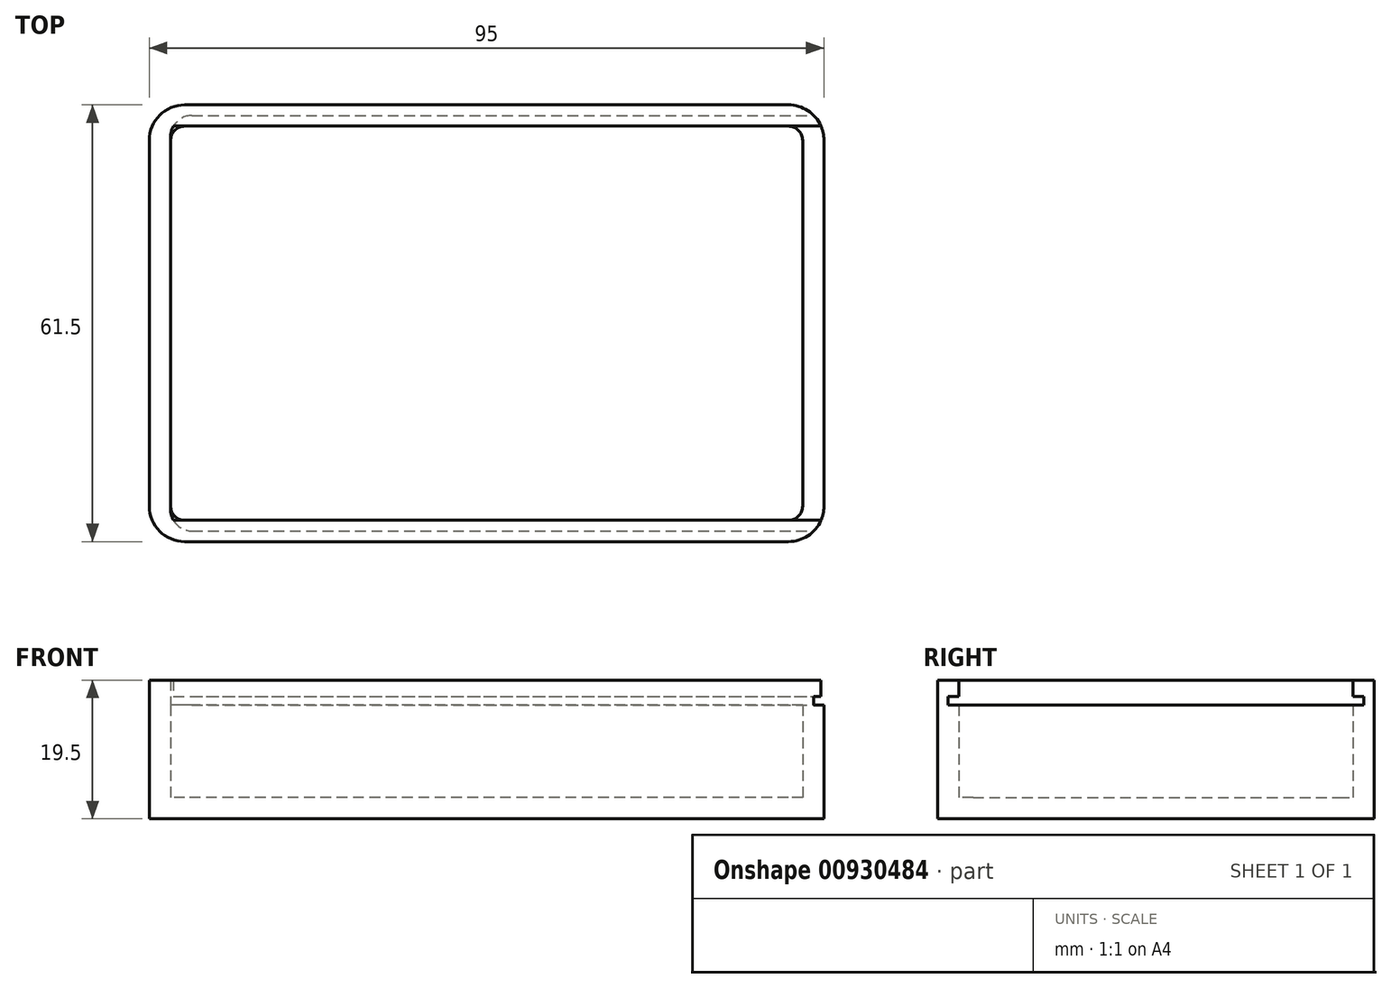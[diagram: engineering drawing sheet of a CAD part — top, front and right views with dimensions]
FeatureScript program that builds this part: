
annotation { "Feature Type Name" : "Feature", "Feature Type Description" : "" }
export const myFeature = defineFeature(function(context is Context, id is Id, definition is map)
    precondition{}
    {
        {
            var Q0;
            Q0=qCreatedBy(makeId("Top.planeOp"),FACE);
            var sketch = newSketch(context, id + "F0", { "sketchPlane" : qUnion([Q0])});
            skLineSegment(sketch, "E0.bottom", {"start": v(44.5, -27.75) * mm, "end": v(-44.5, -27.75) * mm});
            skLineSegment(sketch, "E0.top", {"start": v(44.5, 27.75) * mm, "end": v(-44.5, 27.75) * mm});
            skLineSegment(sketch, "E0.left", {"start": v(44.5, -27.75) * mm, "end": v(44.5, 27.75) * mm});
            skLineSegment(sketch, "E0.right", {"start": v(-44.5, -27.75) * mm, "end": v(-44.5, 27.75) * mm});
            skPoint(sketch, "E0.middle", {"position": v(0, 0) * mm});
            skLineSegment(sketch, "E1.0", {"start": v(47.5, -30.75) * mm, "end": v(47.5, 30.75) * mm});
            skLineSegment(sketch, "E1.1", {"start": v(47.5, -30.75) * mm, "end": v(-47.5, -30.75) * mm});
            skLineSegment(sketch, "E1.2", {"start": v(-47.5, -30.75) * mm, "end": v(-47.5, 30.75) * mm});
            skLineSegment(sketch, "E1.3", {"start": v(47.5, 30.75) * mm, "end": v(-47.5, 30.75) * mm});
            skSolve(sketch);
        }
        {
            var Q0;
            Q0=makeQuery(id+"F0.imprint","IMPRINT",FACE,{"disambiguationData":[TD([[makeQuery(id+"F0.imprint","IMPRINT",EDGE,{"derivedFrom":sQuery(id+"F0.wireOp",EDGE,"E0.bottom")}),-1.0]])]});
            extrude(context, id + "F1", {"entities" : qUnion([Q0]), "depth" : 3 * mm, "offsetDistance" : 25 * mm});
        }
        {
            var Q0;
            Q0=makeQuery(id+"F0.imprint","IMPRINT",FACE,{"disambiguationData":[TD([[makeQuery(id+"F0.imprint","IMPRINT",EDGE,{"derivedFrom":sQuery(id+"F0.wireOp",EDGE,"E0.bottom")}),1.0]])]});
            extrude(context, id + "F2", {"entities" : qUnion([Q0]), "operationType" : NewBodyOperationType.ADD, "depth" : 16 * mm, "offsetDistance" : 25 * mm});
        }
        {
            var Q0;
            Q0=makeQuery(id+"F2.opExtrude","SWEPT_FACE",FACE,{"disambiguationData":[OSD([sQuery(id+"F0.wireOp",EDGE,"E1.0")])]});
            var sketch = newSketch(context, id + "F3", { "sketchPlane" : qUnion([Q0])});
            skLineSegment(sketch, "E2.top", {"start": v(30.75, 16) * mm, "end": v(27.75, 16) * mm});
            skLineSegment(sketch, "E3.top", {"start": v(30.75, 19.5) * mm, "end": v(27.75, 19.5) * mm});
            skLineSegment(sketch, "E3.left", {"start": v(30.75, 16) * mm, "end": v(30.75, 19.5) * mm});
            skLineSegment(sketch, "E3.right", {"start": v(27.75, 17.2) * mm, "end": v(27.75, 19.5) * mm});
            skLineSegment(sketch, "E4", {"start": v(29.6, 17.2) * mm, "end": v(24.82, 17.2) * mm, "construction": true});
            skLineSegment(sketch, "E5", {"start": v(27.75, 17.2) * mm, "end": v(29.25, 17.2) * mm});
            skPoint(sketch, "E5.startSnap0", {"position": v(27.75, 17.75) * mm});
            skLineSegment(sketch, "E6", {"start": v(29.25, 17.2) * mm, "end": v(29.25, 16) * mm});
            skLineSegment(sketch, "E7", {"start": v(0, 27.37) * mm, "end": v(0, -23.35) * mm, "construction": true});
            skLineSegment(sketch, "E8.MirrorCS", {"start": v(-27.75, 17.2) * mm, "end": v(-29.25, 17.2) * mm});
            skLineSegment(sketch, "E9.MirrorCS", {"start": v(-29.25, 17.2) * mm, "end": v(-29.25, 16) * mm});
            skLineSegment(sketch, "E10.MirrorCS", {"start": v(-30.75, 16) * mm, "end": v(-30.75, 19.5) * mm});
            skLineSegment(sketch, "E11.MirrorCS", {"start": v(-30.75, 16) * mm, "end": v(-27.75, 16) * mm});
            skLineSegment(sketch, "E12.MirrorCS", {"start": v(-27.75, 17.2) * mm, "end": v(-27.75, 19.5) * mm});
            skLineSegment(sketch, "E13.MirrorCS", {"start": v(-29.6, 17.2) * mm, "end": v(-24.82, 17.2) * mm, "construction": true});
            skPoint(sketch, "E14.MirrorP", {"position": v(-27.75, 17.75) * mm});
            skLineSegment(sketch, "E15.MirrorCS", {"start": v(-30.75, 19.5) * mm, "end": v(-27.75, 19.5) * mm});
            skLineSegment(sketch, "E16.trimOffspring", {"start": v(-27.75, 16) * mm, "end": v(-30.75, 16) * mm});
            skSolve(sketch);
        }
        {
            var Q0;
            Q0 = qSketchRegion(id + "F3", true);
            var Q1;
            Q1=makeQuery(id+"F2.opExtrude","SWEPT_FACE",FACE,{"disambiguationData":[OSD([sQuery(id+"F0.wireOp",EDGE,"E1.2")])]});
            extrude(context, id + "F4", {"entities" : qUnion([Q0]), "operationType" : NewBodyOperationType.ADD, "endBound" : BoundingType.UP_TO_SURFACE, "oppositeDirection" : true, "depth" : 25 * mm, "endBoundEntityFace" : qUnion([Q1]), "offsetDistance" : 25 * mm});
        }
        {
            var Q0;
            Q0=makeQuery(id+"F4.boolean.opBoolean","MERGE",FACE,{"derivedFrom":[makeQuery(id+"F2.opExtrude","SWEPT_FACE",FACE,{"disambiguationData":[OSD([sQuery(id+"F0.wireOp",EDGE,"E1.2")])]}),makeQuery(id+"F4.opExtrude","CAP_FACE",FACE,{"disambiguationData":[OSD([sQuery(id+"F3.wireOp",EDGE,"E2.top"),sQuery(id+"F3.wireOp",EDGE,"E3.top"),sQuery(id+"F3.wireOp",EDGE,"E3.left"),sQuery(id+"F3.wireOp",EDGE,"E3.right"),sQuery(id+"F3.wireOp",EDGE,"E5"),sQuery(id+"F3.wireOp",EDGE,"E6")])],"isStart":false}),makeQuery(id+"F4.opExtrude","CAP_FACE",FACE,{"disambiguationData":[OSD([sQuery(id+"F3.wireOp",EDGE,"E8.MirrorCS"),sQuery(id+"F3.wireOp",EDGE,"E9.MirrorCS"),sQuery(id+"F3.wireOp",EDGE,"E10.MirrorCS"),sQuery(id+"F3.wireOp",EDGE,"E12.MirrorCS"),sQuery(id+"F3.wireOp",EDGE,"E15.MirrorCS"),sQuery(id+"F3.wireOp",EDGE,"E16.trimOffspring")])],"isStart":false})]});
            var sketch = newSketch(context, id + "F5", { "sketchPlane" : qUnion([Q0])});
            skLineSegment(sketch, "E17.bottom", {"start": v(-30.75, 19.5) * mm, "end": v(30.75, 19.5) * mm});
            skLineSegment(sketch, "E17.top", {"start": v(-30.75, 16) * mm, "end": v(30.75, 16) * mm});
            skLineSegment(sketch, "E17.left", {"start": v(-30.75, 19.5) * mm, "end": v(-30.75, 16) * mm});
            skLineSegment(sketch, "E17.right", {"start": v(30.75, 19.5) * mm, "end": v(30.75, 16) * mm});
            skSolve(sketch);
        }
        {
            var Q0;
            Q0 = qSketchRegion(id + "F5", true);
            var Q1;
            Q1=makeQuery(id+"F2.opExtrude","SWEPT_FACE",FACE,{"disambiguationData":[OSD([sQuery(id+"F0.wireOp",EDGE,"E0.right")])]});
            extrude(context, id + "F6", {"entities" : qUnion([Q0]), "operationType" : NewBodyOperationType.ADD, "oppositeDirection" : true, "depth" : 3 * mm, "endBoundEntityFace" : qUnion([Q1]), "offsetDistance" : 25 * mm});
        }
        {
            var Q0;
            Q0=makeQuery(id+"F4.boolean.opBoolean","MERGE",EDGE,{"derivedFrom":[makeQuery(id+"F2.opExtrude","SWEPT_EDGE",EDGE,{"disambiguationData":[OSD([sQuery(id+"F0.wireOp",EDGE,"E1.0"),sQuery(id+"F0.wireOp",EDGE,"E1.1")])]}),makeQuery(id+"F4.opExtrude","CAP_EDGE",EDGE,{"disambiguationData":[OSD([sQuery(id+"F3.wireOp",EDGE,"E10.MirrorCS")])],"isStart":true})]});
            var Q1;
            Q1=makeQuery(id+"F4.boolean.opBoolean","MERGE",EDGE,{"derivedFrom":[makeQuery(id+"F2.opExtrude","SWEPT_EDGE",EDGE,{"disambiguationData":[OSD([sQuery(id+"F0.wireOp",EDGE,"E1.1"),sQuery(id+"F0.wireOp",EDGE,"E1.2")])]}),makeQuery(id+"F4.opExtrude","CAP_EDGE",EDGE,{"disambiguationData":[OSD([sQuery(id+"F3.wireOp",EDGE,"E10.MirrorCS")])],"isStart":false})]});
            var Q2;
            Q2=makeQuery(id+"F4.boolean.opBoolean","MERGE",EDGE,{"derivedFrom":[makeQuery(id+"F2.opExtrude","SWEPT_EDGE",EDGE,{"disambiguationData":[OSD([sQuery(id+"F0.wireOp",EDGE,"E1.0"),sQuery(id+"F0.wireOp",EDGE,"E1.3")])]}),makeQuery(id+"F4.opExtrude","CAP_EDGE",EDGE,{"disambiguationData":[OSD([sQuery(id+"F3.wireOp",EDGE,"E3.left")])],"isStart":true})]});
            var Q3;
            Q3=makeQuery(id+"F4.boolean.opBoolean","MERGE",EDGE,{"derivedFrom":[makeQuery(id+"F2.opExtrude","SWEPT_EDGE",EDGE,{"disambiguationData":[OSD([sQuery(id+"F0.wireOp",EDGE,"E1.2"),sQuery(id+"F0.wireOp",EDGE,"E1.3")])]}),makeQuery(id+"F4.opExtrude","CAP_EDGE",EDGE,{"disambiguationData":[OSD([sQuery(id+"F3.wireOp",EDGE,"E3.left")])],"isStart":false})]});
            fillet(context, id + "F7", {"entities" : qUnion([Q0, Q1, Q2, Q3]), "radius" : 5 * mm, "tangentPropagation" : true, "allowEdgeOverflow" : false});
        }
        {
            var Q0;
            Q0=makeQuery(id+"F2.opExtrude","SWEPT_EDGE",EDGE,{"disambiguationData":[OSD([sQuery(id+"F0.wireOp",EDGE,"E0.top"),sQuery(id+"F0.wireOp",EDGE,"E0.right")])]});
            var Q1;
            Q1=makeQuery(id+"F2.opExtrude","SWEPT_EDGE",EDGE,{"disambiguationData":[OSD([sQuery(id+"F0.wireOp",EDGE,"E0.bottom"),sQuery(id+"F0.wireOp",EDGE,"E0.right")])]});
            var Q2;
            Q2=makeQuery(id+"F2.opExtrude","SWEPT_EDGE",EDGE,{"disambiguationData":[OSD([sQuery(id+"F0.wireOp",EDGE,"E0.bottom"),sQuery(id+"F0.wireOp",EDGE,"E0.left")])]});
            var Q3;
            Q3=makeQuery(id+"F2.opExtrude","SWEPT_EDGE",EDGE,{"disambiguationData":[OSD([sQuery(id+"F0.wireOp",EDGE,"E0.top"),sQuery(id+"F0.wireOp",EDGE,"E0.left")])]});
            fillet(context, id + "F8", {"entities" : qUnion([Q0, Q1, Q2, Q3]), "radius" : 2 * mm, "tangentPropagation" : true, "allowEdgeOverflow" : false});
        }
        {
            var Q0;
            Q0=makeQuery(id+"F6.boolean.opBoolean","INTERSECT",EDGE,{"derivedFrom":[makeQuery(id+"F4.opExtrude","SWEPT_FACE",FACE,{"disambiguationData":[OSD([sQuery(id+"F3.wireOp",EDGE,"E9.MirrorCS")])]}),makeQuery(id+"F6.opExtrude","CAP_FACE",FACE,{"disambiguationData":[OSD([sQuery(id+"F5.wireOp",EDGE,"E17.bottom"),sQuery(id+"F5.wireOp",EDGE,"E17.top"),sQuery(id+"F5.wireOp",EDGE,"E17.left"),sQuery(id+"F5.wireOp",EDGE,"E17.right")])],"isStart":false})]});
            var Q1;
            Q1=makeQuery(id+"F6.boolean.opBoolean","INTERSECT",EDGE,{"derivedFrom":[makeQuery(id+"F4.opExtrude","SWEPT_FACE",FACE,{"disambiguationData":[OSD([sQuery(id+"F3.wireOp",EDGE,"E6")])]}),makeQuery(id+"F6.opExtrude","CAP_FACE",FACE,{"disambiguationData":[OSD([sQuery(id+"F5.wireOp",EDGE,"E17.bottom"),sQuery(id+"F5.wireOp",EDGE,"E17.top"),sQuery(id+"F5.wireOp",EDGE,"E17.left"),sQuery(id+"F5.wireOp",EDGE,"E17.right")])],"isStart":false})]});
            fillet(context, id + "F9", {"entities" : qUnion([Q0, Q1]), "radius" : 3 * mm, "tangentPropagation" : true, "allowEdgeOverflow" : false});
        }
    });
